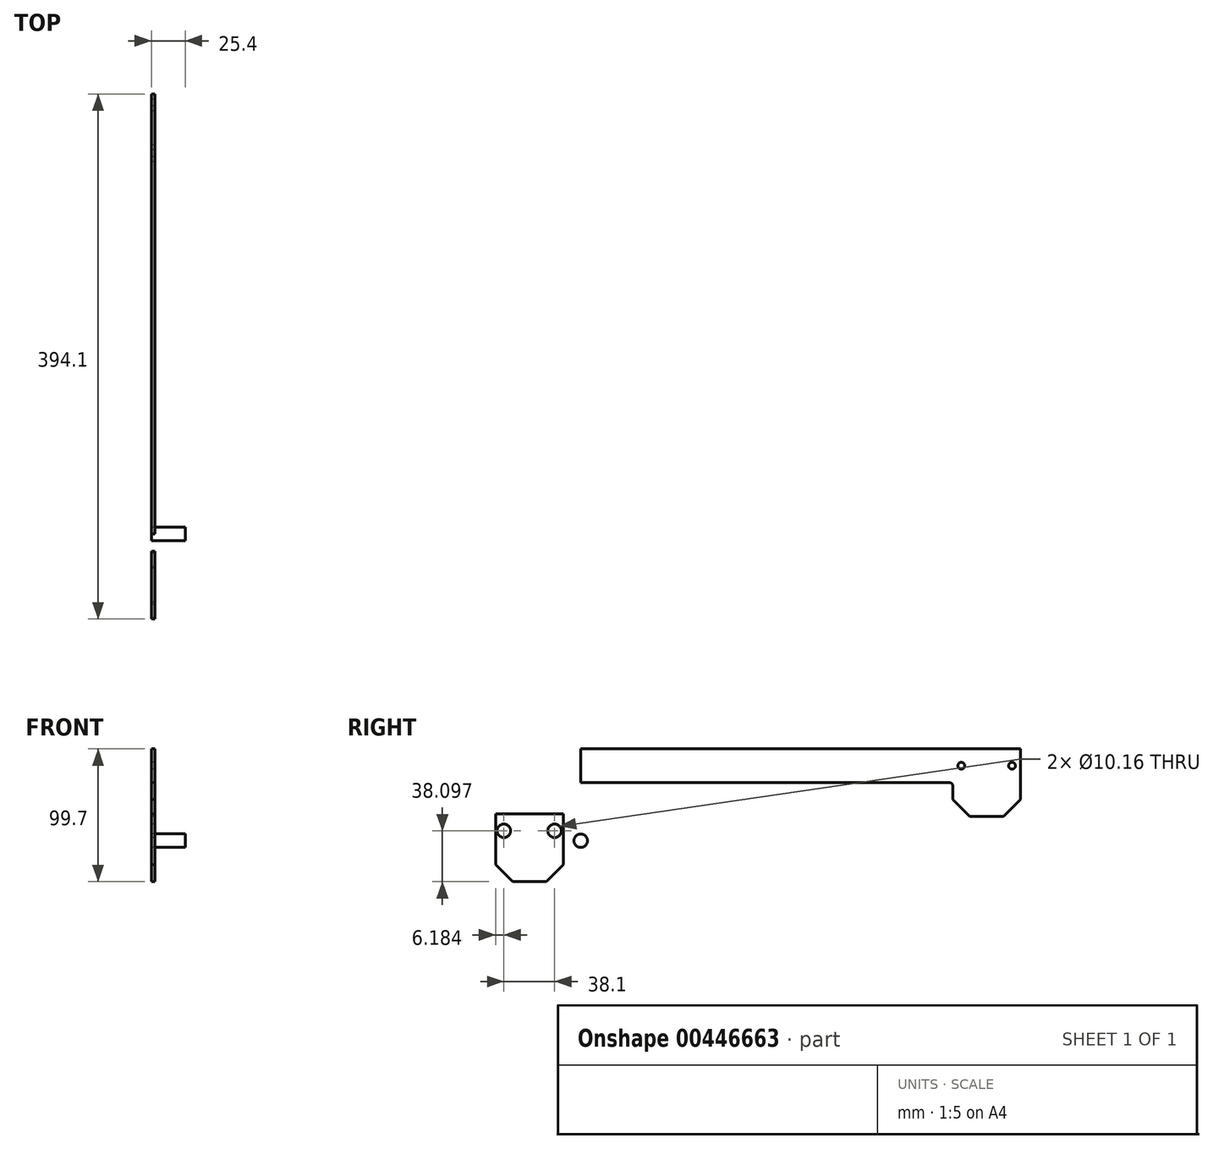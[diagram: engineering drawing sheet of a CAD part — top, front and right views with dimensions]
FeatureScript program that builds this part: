
annotation { "Feature Type Name" : "Feature", "Feature Type Description" : "" }
export const myFeature = defineFeature(function(context is Context, id is Id, definition is map)
    precondition{}
    {
        {
            var Q0;
            Q0=qCreatedBy(makeId("Right.planeOp"),FACE);
            var sketch = newSketch(context, id + "F0", { "sketchPlane" : qUnion([Q0])});
            skLineSegment(sketch, "E0.bottom", {"start": v(0, 0) * mm, "end": v(276.86, 0) * mm});
            skLineSegment(sketch, "E0.top", {"start": v(0, 25.4) * mm, "end": v(330.2, 25.4) * mm});
            skLineSegment(sketch, "E0.left", {"start": v(0, 0) * mm, "end": v(0, 25.4) * mm});
            skCircle(sketch, "E1", {"center": v(285.75, 12.7) * mm, "radius": 2.58 * mm});
            skCircle(sketch, "E2", {"center": v(323.85, 12.7) * mm, "radius": 2.58 * mm});
            skCircle(sketch, "E3", {"center": v(0, -43.6) * mm, "radius": 5.08 * mm});
            skPoint(sketch, "E3.centerSnap0", {"position": v(0, 12.7) * mm});
            skLineSegment(sketch, "E4.bottom", {"start": v(-63.9, -23.5) * mm, "end": v(-13.1, -23.5) * mm});
            skLineSegment(sketch, "E4.top", {"start": v(-51.2, -74.3) * mm, "end": v(-25.8, -74.3) * mm});
            skLineSegment(sketch, "E4.left", {"start": v(-63.9, -23.5) * mm, "end": v(-63.9, -61.6) * mm});
            skLineSegment(sketch, "E4.right", {"start": v(-13.1, -23.5) * mm, "end": v(-13.1, -61.6) * mm});
            skCircle(sketch, "E5", {"center": v(-57.72, -36.2) * mm, "radius": 5.08 * mm});
            skCircle(sketch, "E6", {"center": v(-19.62, -36.2) * mm, "radius": 5.08 * mm});
            skLineSegment(sketch, "E7", {"start": v(-51.2, -74.3) * mm, "end": v(-63.9, -61.6) * mm});
            skLineSegment(sketch, "E8", {"start": v(-25.8, -74.3) * mm, "end": v(-13.1, -61.6) * mm});
            skPoint(sketch, "E9.orphan", {"position": v(-13.1, -74.3) * mm});
            skPoint(sketch, "E10.orphan", {"position": v(-63.9, -74.3) * mm});
            skLineSegment(sketch, "E11.0", {"start": v(292.1, -25.4) * mm, "end": v(317.5, -25.4) * mm});
            skLineSegment(sketch, "E12", {"start": v(279.4, -2.54) * mm, "end": v(279.4, -12.7) * mm});
            skLineSegment(sketch, "E13", {"start": v(330.2, 25.4) * mm, "end": v(330.2, -12.7) * mm});
            skLineSegment(sketch, "E14", {"start": v(317.5, -25.4) * mm, "end": v(330.2, -12.7) * mm});
            skLineSegment(sketch, "E15", {"start": v(292.1, -25.4) * mm, "end": v(279.4, -12.7) * mm});
            skPoint(sketch, "E16.visualSharp", {"position": v(279.4, 0) * mm});
            skArc(sketch, "E16.filletArc", {"start": v(279.4, -2.54) * mm, "mid": v(278.66, -0.74) * mm, "end": v(276.86, 0) * mm});
            skSolve(sketch);
        }
        {
            var Q0;
            Q0=makeQuery(id+"F0.imprint","IMPRINT",FACE,{"disambiguationData":[TD([[makeQuery(id+"F0.imprint","IMPRINT",EDGE,{"derivedFrom":sQuery(id+"F0.wireOp",EDGE,"E0.bottom")}),1.0]])]});
            extrude(context, id + "F1", {"entities" : qUnion([Q0]), "depth" : 2.54 * mm});
        }
        {
            var Q0;
            Q0=makeQuery(id+"F0.imprint","IMPRINT",FACE,{"disambiguationData":[TD([[makeQuery(id+"F0.imprint","IMPRINT",EDGE,{"derivedFrom":sQuery(id+"F0.wireOp",EDGE,"E4.bottom")}),-1.0]])]});
            extrude(context, id + "F2", {"entities" : qUnion([Q0]), "depth" : 2.54 * mm});
        }
        {
            var Q0;
            Q0=makeQuery(id+"F0.imprint","IMPRINT",FACE,{"disambiguationData":[TD([[makeQuery(id+"F0.imprint","IMPRINT",EDGE,{"derivedFrom":sQuery(id+"F0.wireOp",EDGE,"E3")}),1.0]])]});
            extrude(context, id + "F3", {"entities" : qUnion([Q0]), "depth" : 25.4 * mm});
        }
    });
